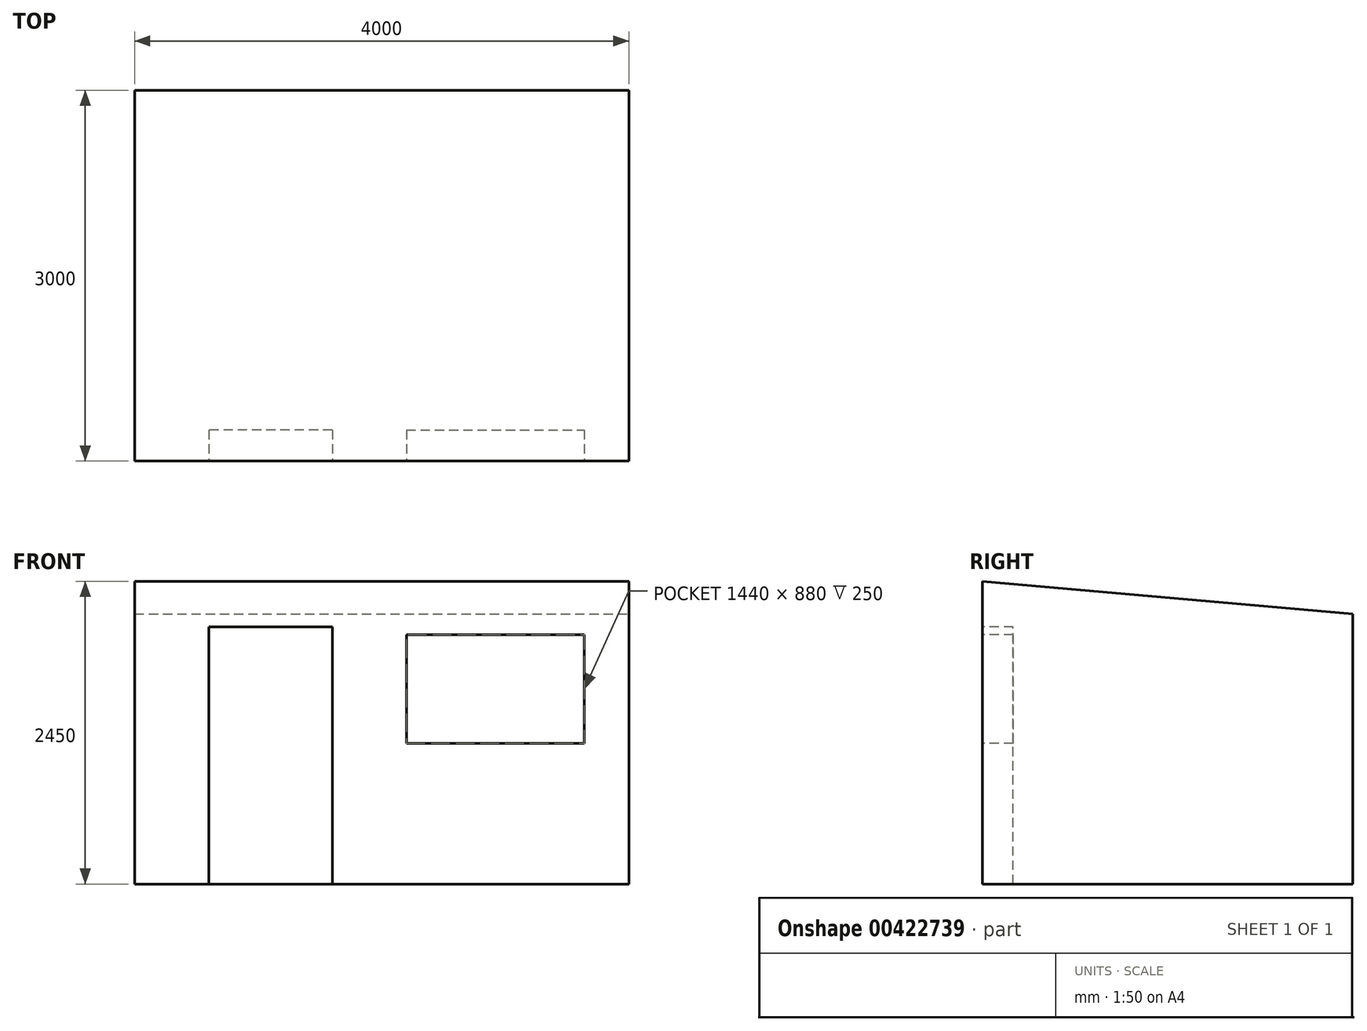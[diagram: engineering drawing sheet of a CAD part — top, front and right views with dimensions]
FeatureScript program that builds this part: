
annotation { "Feature Type Name" : "Feature", "Feature Type Description" : "" }
export const myFeature = defineFeature(function(context is Context, id is Id, definition is map)
    precondition{}
    {
        {
            var Q0;
            Q0=qCreatedBy(makeId("Top.planeOp"),FACE);
            var sketch = newSketch(context, id + "F0", { "sketchPlane" : qUnion([Q0])});
            skLineSegment(sketch, "E0.bottom", {"start": v(2000, -1500) * mm, "end": v(-2000, -1500) * mm});
            skLineSegment(sketch, "E0.top", {"start": v(2000, 1500) * mm, "end": v(-2000, 1500) * mm});
            skLineSegment(sketch, "E0.left", {"start": v(2000, -1500) * mm, "end": v(2000, 1500) * mm});
            skLineSegment(sketch, "E0.right", {"start": v(-2000, -1500) * mm, "end": v(-2000, 1500) * mm});
            skPoint(sketch, "E0.middle", {"position": v(0, 0) * mm});
            skSolve(sketch);
        }
        {
            var Q0;
            Q0 = qSketchRegion(id + "F0", true);
            extrude(context, id + "F1", {"entities" : qUnion([Q0]), "depth" : 2450 * mm});
        }
        {
            var Q0;
            Q0=makeQuery(id+"F1.opExtrude","SWEPT_FACE",FACE,{"disambiguationData":[OSD([sQuery(id+"F0.wireOp",EDGE,"E0.left")])]});
            var sketch = newSketch(context, id + "F2", { "sketchPlane" : qUnion([Q0])});
            skLineSegment(sketch, "E1", {"start": v(-1500, 2450) * mm, "end": v(1500, 2187.53) * mm});
            skLineSegment(sketch, "E2", {"start": v(1500, 2187.53) * mm, "end": v(1500, 2450) * mm});
            skLineSegment(sketch, "E3", {"start": v(1500, 2450) * mm, "end": v(-1500, 2450) * mm});
            skSolve(sketch);
        }
        {
            var Q0;
            Q0=makeQuery(id+"F2.imprint","IMPRINT",FACE,{"disambiguationData":[TD([[makeQuery(id+"F2.imprint","IMPRINT",EDGE,{"derivedFrom":sQuery(id+"F2.wireOp",EDGE,"E1")}),1.0]])]});
            extrude(context, id + "F3", {"entities" : qUnion([Q0]), "operationType" : NewBodyOperationType.REMOVE, "oppositeDirection" : true, "depth" : 4000 * mm});
        }
        {
            var Q0;
            Q0=makeQuery(id+"F1.opExtrude","SWEPT_FACE",FACE,{"disambiguationData":[OSD([sQuery(id+"F0.wireOp",EDGE,"E0.bottom")])]});
            var sketch = newSketch(context, id + "F4", { "sketchPlane" : qUnion([Q0])});
            skLineSegment(sketch, "E4.bottom", {"start": v(-1400, 0) * mm, "end": v(-400, 0) * mm});
            skLineSegment(sketch, "E4.top", {"start": v(-1400, 2080) * mm, "end": v(-400, 2080) * mm});
            skLineSegment(sketch, "E4.left", {"start": v(-1400, 0) * mm, "end": v(-1400, 2080) * mm});
            skLineSegment(sketch, "E4.right", {"start": v(-400, 0) * mm, "end": v(-400, 2080) * mm});
            skLineSegment(sketch, "E5.bottom", {"start": v(199.49, 2017.49) * mm, "end": v(1639.49, 2017.49) * mm});
            skLineSegment(sketch, "E5.top", {"start": v(199.49, 1137.49) * mm, "end": v(1639.49, 1137.49) * mm});
            skLineSegment(sketch, "E5.left", {"start": v(199.49, 2017.49) * mm, "end": v(199.49, 1137.49) * mm});
            skLineSegment(sketch, "E5.right", {"start": v(1639.49, 2017.49) * mm, "end": v(1639.49, 1137.49) * mm});
            skLineSegment(sketch, "E6", {"start": v(2000, 0) * mm, "end": v(2000, 2450) * mm, "construction": true});
            skLineSegment(sketch, "E7", {"start": v(2000, 0) * mm, "end": v(-2000, 0) * mm, "construction": true});
            skSolve(sketch);
        }
        {
            var Q0;
            Q0=makeQuery(id+"F4.imprint","IMPRINT",FACE,{"disambiguationData":[TD([[makeQuery(id+"F4.imprint","IMPRINT",EDGE,{"derivedFrom":sQuery(id+"F4.wireOp",EDGE,"E5.bottom")}),-1.0]])]});
            var Q1;
            Q1=makeQuery(id+"F4.imprint","IMPRINT",FACE,{"disambiguationData":[TD([[makeQuery(id+"F4.imprint","IMPRINT",EDGE,{"derivedFrom":sQuery(id+"F4.wireOp",EDGE,"E4.bottom")}),-1.0]])]});
            extrude(context, id + "F5", {"entities" : qUnion([Q0, Q1]), "operationType" : NewBodyOperationType.REMOVE, "oppositeDirection" : true, "depth" : 250 * mm});
        }
    });
